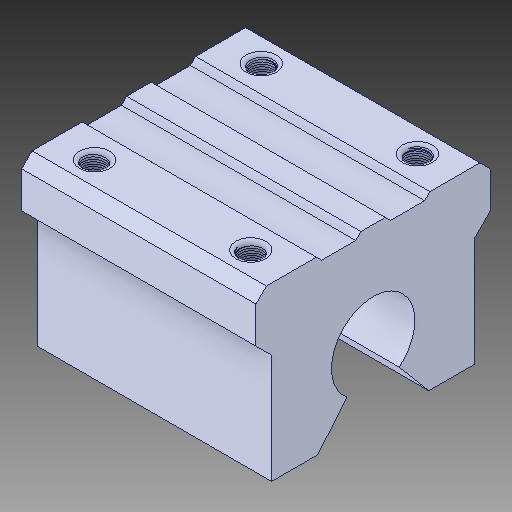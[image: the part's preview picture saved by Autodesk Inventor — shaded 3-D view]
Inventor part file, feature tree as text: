
AUTODESK INVENTOR PART (.ipt)
format: ipt  version: 2018 (Build 220112000, 112)  size: 793,600 bytes
history: native  units: mm
features: other x1, mirror x1
ambient origin geometry x8: Origin, YZ Plane, XZ Plane, XY Plane, X Axis, Y Axis, Z Axis, Center Point
bodies: Body1 (feature_tree)
feature tree (2):
  other  "Sólido1"
  mirror  "Mirror2"
